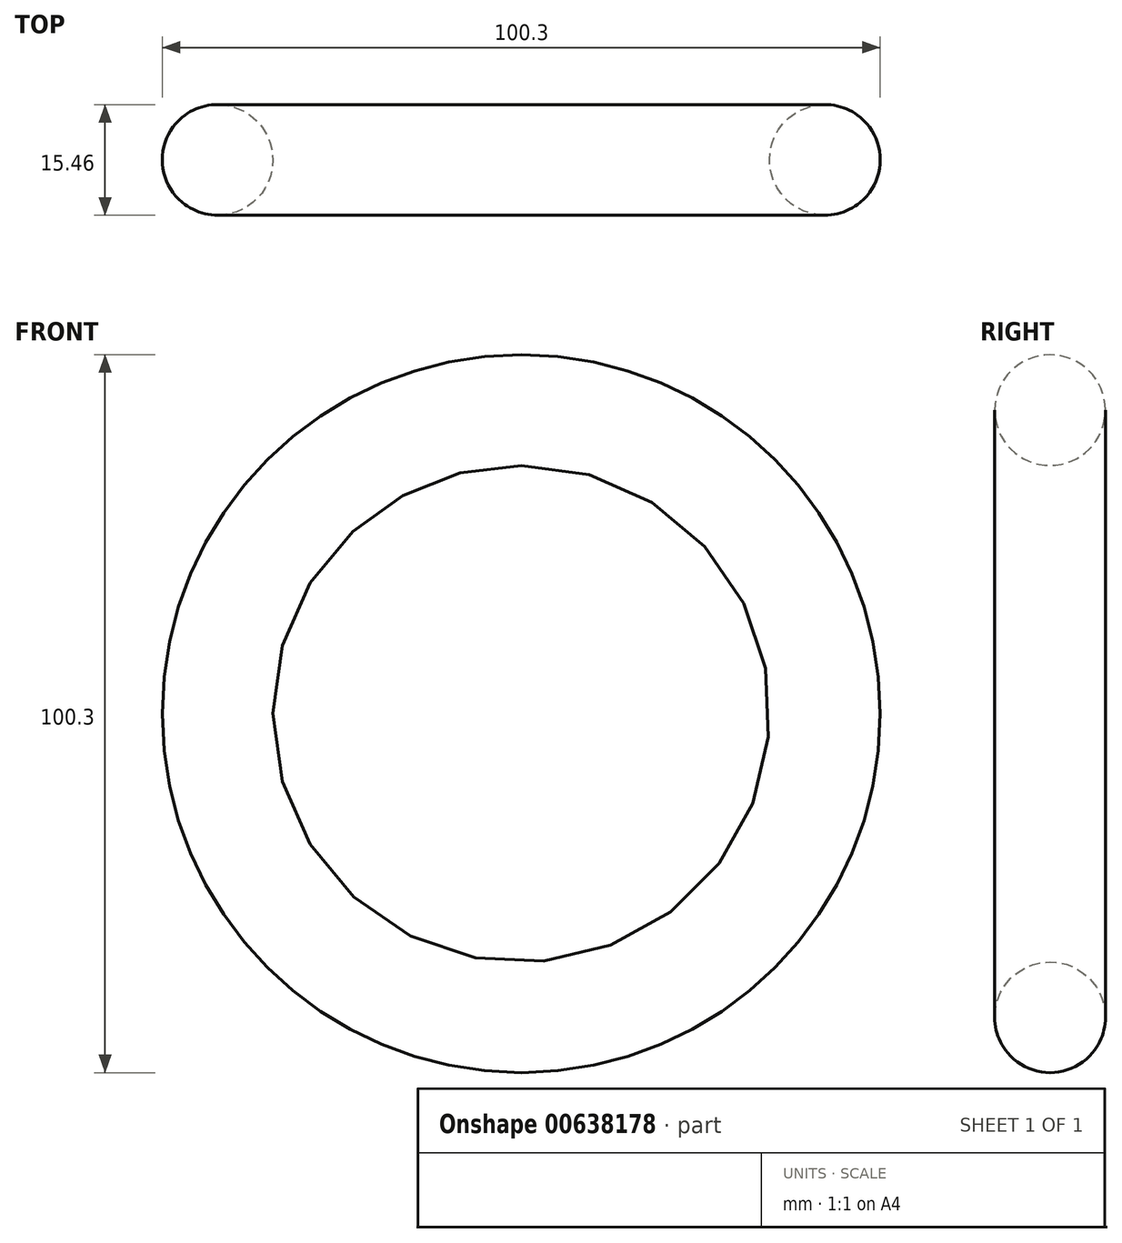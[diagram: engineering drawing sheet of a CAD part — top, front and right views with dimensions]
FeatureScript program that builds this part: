
annotation { "Feature Type Name" : "Feature", "Feature Type Description" : "" }
export const myFeature = defineFeature(function(context is Context, id is Id, definition is map)
    precondition{}
    {
        {
            var Q0;
            Q0=qCreatedBy(makeId("Top.planeOp"),FACE);
            var sketch = newSketch(context, id + "F0", { "sketchPlane" : qUnion([Q0])});
            skCircle(sketch, "E0", {"center": v(42.42, 0) * mm, "radius": 7.73 * mm});
            skSolve(sketch);
        }
        {
            var Q0;
            Q0=qCreatedBy(makeId("Top.planeOp"),FACE);
            var sketch = newSketch(context, id + "F1", { "sketchPlane" : qUnion([Q0])});
            skLineSegment(sketch, "E1", {"start": v(0, 12.12) * mm, "end": v(0, -18.2) * mm});
            skSolve(sketch);
        }
        {
            var Q0;
            Q0 = qSketchRegion(id + "F0", true);
            var Q1;
            Q1=sQuery(id+"F1.wireOp",EDGE,"E1");
            revolve(context, id + "F2", {"entities" : qUnion([Q0]), "axis" : qUnion([Q1]), "revolveType" : RevolveType.FULL});
        }
    });
